# Revit family: Hager-SM_Design_30-RCCB_Incomer-NoHosted-UK-en
name_source: partatom
category: Electrical Equipment
units: mm (PartAtom-declared; Revit-internal decimal feet)

## family parameters
Always vertical = Yes
Cut with Voids When Loaded = No
Panel Configuration = Two Columns, Circuits Across
Part Type = Panelboard
Room Calculation Point = No
Round Connector Dimension = Use Diameter
Shared = No
Work Plane-Based = Yes

## types (9) — shared parameters
Classification.Uniclass.Pr.Description = Control circuit device enclosures
Classification.Uniclass.Pr.Number = Pr_80_77_28_16
Default Elevation = 1219 mm
EF000003 - Mounting method = EV000384 - Surface mounted (plaster)
EF000040 - Height = 240 mm  [stored 0.787402 ft]
EF000049 - Depth = 102 mm
EF000116 - RAL-number = 9010
EF000118 - With mounting plate = No
EF000266 - Number of rows = 1
EF000339 - Type of cover = EV004216 - Door
EF001062 - EMC-version = No
EF001088 - Extension possible = Yes
EF001134 - DIN-rail = No
EF001596 - Material housing = EV000179 - Steel
EF004462 - Type of closure = EV000154 - Other
EF005474 - Degree of protection (IP) = EV009848 - IP2XC
EF006244 - Transparent cover/door = No
EF006306 - With lock = No
EF015776 - Earthing terminal block = Yes
EF015777 - Neutral terminal block = Yes
EF015941 - Signal passing door = No
HG000002 - With door or cover = Yes
HG000003 - Range = Surface Mounting Consumer Units
HG000005 - Thickness = 3 mm  [stored 0.00984252 ft]
HG000006 - Flush mounted = No
HG000017 - Distance between poles = 18 mm  [stored 0.0590551 ft]
Manufacturer = Hager
Type Comments = Surface Mounting Consumer Units
zero-valued in all types: Cost, EF000218 - Built-in depth, EF000332 - Built-in height, EF000846 - Built-in width, EF001131 - Internal depth

## per-type parameters (varying)
| type | EF000008 - Width | EF002950 - Width in number of modular spacings | HG000004 - Manufacturer reference | Model |
| Surface mounted P2XC W149 H240 D102 2 Modular spacings - VM402AH | 149 mm  [stored 0.488845 ft] | 2 | VM402AH | VM402AH |
| Surface mounted P2XC W149 H240 D102 4 Modular spacings - VM24AH | 149 mm  [stored 0.488845 ft] | 4 | VM24AH | VM24AH |
| Surface mounted P2XC W149 H240 D102 4 Modular spacings - VM24AHK | 149 mm  [stored 0.488845 ft] | 4 | VM24AHK | VM24AHK |
| Surface mounted P2XC W221 H240 D102 6 Modular spacings - VM306AH | 221 mm  [stored 0.725066 ft] | 6 | VM306AH | VM306AH |
| Surface mounted P2XC W221 H240 D102 6 Modular spacings - VM406AH | 221 mm  [stored 0.725066 ft] | 6 | VM406AH | VM406AH |
| Surface mounted P2XC W221 H240 D102 6 Modular spacings - VM406AHK | 221 mm  [stored 0.725066 ft] | 6 | VM406AHK | VM406AHK |
| Surface mounted P2XC W292 H240 D102 10 Modular spacings - VM410AH | 292 mm  [stored 0.958005 ft] | 10 | VM410AH | VM410AH |
| Surface mounted P2XC W292 H240 D102 10 Modular spacings - VM410AHK | 292 mm  [stored 0.958005 ft] | 10 | VM410AHK | VM410AHK |
| Surface mounted P2XC W364 H240 D102 14 Modular spacings - VM314AH | 364 mm  [stored 1.19423 ft] | 14 | VM314AH | VM314AH |

note: [stored X ft] marks values corroborated as IEEE doubles in the binary element streams (Revit-internal decimal feet)

## geometry (parser evidence)
native form markers: Blend x4, Sweep x13
no freeform markers — native parametric forms only
